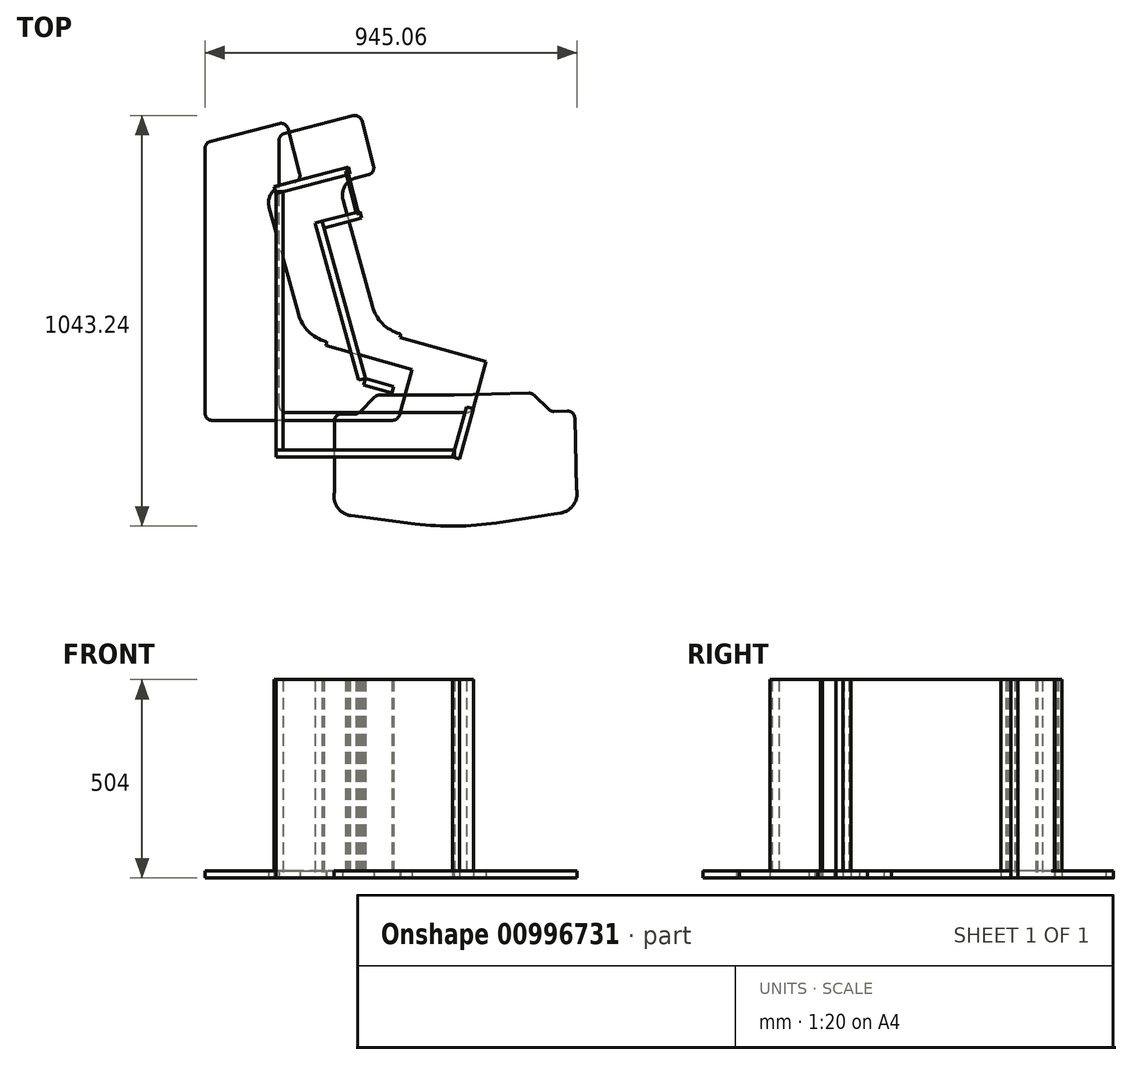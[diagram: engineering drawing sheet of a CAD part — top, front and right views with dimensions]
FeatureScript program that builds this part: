
annotation { "Feature Type Name" : "Feature", "Feature Type Description" : "" }
export const myFeature = defineFeature(function(context is Context, id is Id, definition is map)
    precondition{}
    {
        {
            var Q0;
            Q0=qCreatedBy(makeId("Top.planeOp"),FACE);
            var sketch = newSketch(context, id + "F0", { "sketchPlane" : qUnion([Q0])});
            skLineSegment(sketch, "E0", {"start": v(6.37, 0) * mm, "end": v(-452, 0) * mm});
            skLineSegment(sketch, "E1", {"start": v(-470, 18) * mm, "end": v(-470, 691.14) * mm});
            skArc(sketch, "E2.filletArc", {"start": v(-470, 18) * mm, "mid": v(-464.73, 5.27) * mm, "end": v(-452, 0) * mm});
            skPoint(sketch, "E3.visualSharp", {"position": v(-325.33, 755) * mm});
            skLineSegment(sketch, "E4", {"start": v(-470, 18) * mm, "end": v(-470, 379.49) * mm});
            skLineSegment(sketch, "E5", {"start": v(-470, 379.49) * mm, "end": v(-470, 508.49) * mm});
            skLineSegment(sketch, "E6", {"start": v(-307.17, 540.54) * mm, "end": v(-232.7, 269.91) * mm});
            skLineSegment(sketch, "E7", {"start": v(-264.5, 385.5) * mm, "end": v(-300, 514.5) * mm});
            skLineSegment(sketch, "E8", {"start": v(-470, 18) * mm, "end": v(-470, 175.49) * mm});
            skLineSegment(sketch, "E9", {"start": v(56.32, 128.98) * mm, "end": v(23.7, 13.12) * mm});
            skPoint(sketch, "E10.visualSharp", {"position": v(20, 0) * mm});
            skPoint(sketch, "E11.orphan", {"position": v(-70.83, 811.56) * mm});
            skLineSegment(sketch, "E12.0", {"start": v(-455, 27) * mm, "end": v(-455, 683.67) * mm, "construction": true});
            skLineSegment(sketch, "E13.0", {"start": v(-459.52, 696.42) * mm, "end": v(-270.78, 745.42) * mm, "construction": true});
            skLineSegment(sketch, "E14.0", {"start": v(-456.52, 708.56) * mm, "end": v(-281.29, 754.05) * mm});
            skLineSegment(sketch, "E15", {"start": v(-459.52, 696.42) * mm, "end": v(-455, 679) * mm, "construction": true});
            skLineSegment(sketch, "E16.0", {"start": v(-437, 27) * mm, "end": v(-437, 679) * mm, "construction": true});
            skLineSegment(sketch, "E17", {"start": v(-455, 679) * mm, "end": v(-437, 679) * mm, "construction": true});
            skPoint(sketch, "E18.visualSharp", {"position": v(-470, 705.06) * mm});
            skArc(sketch, "E18.filletArc", {"start": v(-456.52, 708.56) * mm, "mid": v(-466.24, 702.15) * mm, "end": v(-470, 691.14) * mm});
            skLineSegment(sketch, "E19", {"start": v(-237.1, 615.72) * mm, "end": v(-270.78, 745.42) * mm, "construction": true});
            skLineSegment(sketch, "E20.0", {"start": v(-229.56, 626.46) * mm, "end": v(-259.34, 741.15) * mm});
            skPoint(sketch, "E21.visualSharp", {"position": v(-263.87, 758.58) * mm});
            skArc(sketch, "E21.filletArc", {"start": v(-259.34, 741.15) * mm, "mid": v(-267.64, 752.15) * mm, "end": v(-281.29, 754.05) * mm});
            skLineSegment(sketch, "E22", {"start": v(-266.26, 728) * mm, "end": v(-271.1, 726.74) * mm, "construction": true});
            skLineSegment(sketch, "E23.0", {"start": v(-275.09, 596.04) * mm, "end": v(-242.46, 604.51) * mm});
            skLineSegment(sketch, "E24.0", {"start": v(-332.94, 590.84) * mm, "end": v(-237.1, 615.72) * mm, "construction": true});
            skLineSegment(sketch, "E25.0", {"start": v(-355.14, 603.67) * mm, "end": v(-251.31, 630.63) * mm, "construction": true});
            skLineSegment(sketch, "E26.0", {"start": v(-337.71, 608.2) * mm, "end": v(-227.85, 209) * mm, "construction": true});
            skLineSegment(sketch, "E27.0", {"start": v(-355.07, 603.42) * mm, "end": v(-245.28, 204.47) * mm, "construction": true});
            skPoint(sketch, "E28.visualSharp", {"position": v(-225.04, 609.03) * mm});
            skArc(sketch, "E28.filletArc", {"start": v(-242.46, 604.51) * mm, "mid": v(-231.47, 612.81) * mm, "end": v(-229.56, 626.46) * mm});
            skPoint(sketch, "E29.visualSharp", {"position": v(-319.28, 584.57) * mm});
            skArc(sketch, "E30.filletArc", {"start": v(-275.09, 596.04) * mm, "mid": v(-302.74, 575) * mm, "end": v(-307.17, 540.54) * mm});
            skLineSegment(sketch, "E31.0", {"start": v(-245.28, 204.47) * mm, "end": v(-227.85, 209) * mm, "construction": true});
            skLineSegment(sketch, "E32", {"start": v(-160, 189.88) * mm, "end": v(-155.66, 188.66) * mm});
            skLineSegment(sketch, "E33.0", {"start": v(-232.73, 191.66) * mm, "end": v(-160.54, 171.34) * mm, "construction": true});
            skLineSegment(sketch, "E34", {"start": v(-227.85, 209) * mm, "end": v(-155.66, 188.66) * mm, "construction": true});
            skLineSegment(sketch, "E35", {"start": v(-227.85, 209) * mm, "end": v(-232.73, 191.66) * mm, "construction": true});
            skLineSegment(sketch, "E36.0", {"start": v(-163.8, 200.3) * mm, "end": v(-163.38, 200.19) * mm});
            skLineSegment(sketch, "E37", {"start": v(-155.66, 188.66) * mm, "end": v(-160.54, 171.34) * mm, "construction": true});
            skLineSegment(sketch, "E38", {"start": v(-155.66, 188.66) * mm, "end": v(56.32, 128.98) * mm});
            skArc(sketch, "E39.filletArc", {"start": v(-232.7, 269.91) * mm, "mid": v(-207.2, 225.94) * mm, "end": v(-163.38, 200.19) * mm});
            skLineSegment(sketch, "E40.0", {"start": v(-162.43, 197.84) * mm, "end": v(-164.32, 191.1) * mm});
            skLineSegment(sketch, "E41.0", {"start": v(46.7, 131.7) * mm, "end": v(10.77, 4.11) * mm, "construction": true});
            skArc(sketch, "E42.filletArc", {"start": v(6.37, 0) * mm, "mid": v(17.24, 3.65) * mm, "end": v(23.7, 13.12) * mm});
            skLineSegment(sketch, "E43.0", {"start": v(29.36, 136.57) * mm, "end": v(-6.56, 9) * mm, "construction": true});
            skLineSegment(sketch, "E44", {"start": v(-160.54, 171.34) * mm, "end": v(-160.54, 171.34) * mm});
            skLineSegment(sketch, "E45", {"start": v(-455, 27) * mm, "end": v(-455, 9) * mm, "construction": true});
            skLineSegment(sketch, "E46.0", {"start": v(-1.49, 9) * mm, "end": v(-455, 9) * mm, "construction": true});
            skLineSegment(sketch, "E47.0", {"start": v(-7, 27) * mm, "end": v(-7, 9) * mm, "construction": true});
            skLineSegment(sketch, "E48", {"start": v(-437, 679) * mm, "end": v(-437, 683.67) * mm, "construction": true});
            skLineSegment(sketch, "E49", {"start": v(-1.49, 27) * mm, "end": v(-455, 27) * mm, "construction": true});
            skLineSegment(sketch, "E50", {"start": v(-1.49, 27) * mm, "end": v(-1.49, 9) * mm, "construction": true});
            skLineSegment(sketch, "E51", {"start": v(-6.56, 9) * mm, "end": v(10.77, 4.11) * mm, "construction": true});
            skLineSegment(sketch, "E52", {"start": v(-437, 683.67) * mm, "end": v(-455, 683.67) * mm, "construction": true});
            skLineSegment(sketch, "E53", {"start": v(-1.49, 9) * mm, "end": v(12.14, 9) * mm, "construction": true});
            skLineSegment(sketch, "E54.0", {"start": v(-241.95, 614.46) * mm, "end": v(-275.62, 744.16) * mm, "construction": true});
            skLineSegment(sketch, "E55.0", {"start": v(-246.79, 613.2) * mm, "end": v(-280.46, 742.9) * mm, "construction": true});
            skLineSegment(sketch, "E56", {"start": v(-246.47, 631.88) * mm, "end": v(-241.63, 633.14) * mm, "construction": true});
            skLineSegment(sketch, "E57", {"start": v(-275.94, 725.48) * mm, "end": v(-455, 679) * mm, "construction": true});
            skLineSegment(sketch, "E58.0", {"start": v(-273.6, 736.42) * mm, "end": v(-278.45, 735.16) * mm, "construction": true});
            skLineSegment(sketch, "E59.0", {"start": v(-250.05, 625.79) * mm, "end": v(-245.21, 627.04) * mm, "construction": true});
            skLineSegment(sketch, "E60.0", {"start": v(-272.35, 731.58) * mm, "end": v(-277.2, 730.32) * mm, "construction": true});
            skLineSegment(sketch, "E61", {"start": v(-164.32, 191.1) * mm, "end": v(-155.66, 188.66) * mm});
            skPoint(sketch, "E62.visualSharp", {"position": v(-161.88, 199.77) * mm});
            skArc(sketch, "E62.filletArc", {"start": v(-162.43, 197.84) * mm, "mid": v(-162.6, 199.36) * mm, "end": v(-163.8, 200.3) * mm});
            skSolve(sketch);
        }
        {
            var Q0;
            Q0=qCreatedBy(makeId("Top.planeOp"),FACE);
            var sketch = newSketch(context, id + "F1", { "sketchPlane" : qUnion([Q0])});
            skLineSegment(sketch, "E63.0", {"start": v(-227.85, 209) * mm, "end": v(-232.73, 191.66) * mm});
            skLineSegment(sketch, "E64.0", {"start": v(-227.85, 209) * mm, "end": v(-155.66, 188.66) * mm});
            skLineSegment(sketch, "E64.1", {"start": v(-232.73, 191.66) * mm, "end": v(-160.54, 171.34) * mm});
            skLineSegment(sketch, "E64.2", {"start": v(-155.66, 188.66) * mm, "end": v(-160.54, 171.34) * mm});
            skSolve(sketch);
        }
        {
            var Q0;
            Q0=qCreatedBy(makeId("Top.planeOp"),FACE);
            var sketch = newSketch(context, id + "F2", { "sketchPlane" : qUnion([Q0])});
            skLineSegment(sketch, "E65.0", {"start": v(-266.26, 728) * mm, "end": v(-270.78, 745.42) * mm});
            skLineSegment(sketch, "E65.1", {"start": v(-273.6, 736.42) * mm, "end": v(-278.45, 735.16) * mm});
            skLineSegment(sketch, "E65.3", {"start": v(-271.1, 726.74) * mm, "end": v(-273.6, 736.42) * mm});
            skLineSegment(sketch, "E65.4", {"start": v(-275.94, 725.48) * mm, "end": v(-278.45, 735.16) * mm});
            skLineSegment(sketch, "E65.5", {"start": v(-266.26, 728) * mm, "end": v(-271.1, 726.74) * mm});
            skLineSegment(sketch, "E65.6", {"start": v(-459.52, 696.42) * mm, "end": v(-270.78, 745.42) * mm});
            skLineSegment(sketch, "E65.7", {"start": v(-275.94, 725.48) * mm, "end": v(-455, 679) * mm});
            skLineSegment(sketch, "E65.8", {"start": v(-459.52, 696.42) * mm, "end": v(-455, 679) * mm});
            skLineSegment(sketch, "E65.9", {"start": v(-437, 683.67) * mm, "end": v(-455, 683.67) * mm, "construction": true});
            skLineSegment(sketch, "E65.10", {"start": v(-455, 679) * mm, "end": v(-455, 683.67) * mm, "construction": true});
            skSolve(sketch);
        }
        {
            var Q0;
            Q0=qCreatedBy(makeId("Top.planeOp"),FACE);
            var sketch = newSketch(context, id + "F3", { "sketchPlane" : qUnion([Q0])});
            skLineSegment(sketch, "E66.0", {"start": v(-332.94, 590.84) * mm, "end": v(-237.1, 615.72) * mm});
            skLineSegment(sketch, "E66.1", {"start": v(-337.71, 608.2) * mm, "end": v(-332.94, 590.84) * mm});
            skLineSegment(sketch, "E66.2", {"start": v(-337.71, 608.2) * mm, "end": v(-251.31, 630.63) * mm});
            skLineSegment(sketch, "E66.3", {"start": v(-250.05, 625.79) * mm, "end": v(-251.31, 630.63) * mm});
            skLineSegment(sketch, "E66.4", {"start": v(-245.21, 627.04) * mm, "end": v(-246.47, 631.88) * mm});
            skLineSegment(sketch, "E66.5", {"start": v(-237.1, 615.72) * mm, "end": v(-241.63, 633.14) * mm});
            skLineSegment(sketch, "E66.6", {"start": v(-246.47, 631.88) * mm, "end": v(-241.63, 633.14) * mm});
            skLineSegment(sketch, "E66.7", {"start": v(-250.05, 625.79) * mm, "end": v(-245.21, 627.04) * mm});
            skPoint(sketch, "E67.orphan", {"position": v(-227.85, 209) * mm});
            skSolve(sketch);
        }
        {
            var Q0;
            Q0=qCreatedBy(makeId("Top.planeOp"),FACE);
            var sketch = newSketch(context, id + "F4", { "sketchPlane" : qUnion([Q0])});
            skLineSegment(sketch, "E68.0", {"start": v(-1.49, 27) * mm, "end": v(-455, 27) * mm});
            skLineSegment(sketch, "E68.1", {"start": v(-455, 27) * mm, "end": v(-455, 9) * mm});
            skLineSegment(sketch, "E68.2", {"start": v(-1.49, 9) * mm, "end": v(-455, 9) * mm});
            skLineSegment(sketch, "E68.3", {"start": v(-1.49, 27) * mm, "end": v(-1.49, 9) * mm});
            skLineSegment(sketch, "E68.4", {"start": v(-1.49, 27) * mm, "end": v(-6.56, 9) * mm, "construction": true});
            skPoint(sketch, "E68.5.end.orphan", {"position": v(-7, 9) * mm});
            skSolve(sketch);
        }
        {
            var Q0;
            Q0=qCreatedBy(makeId("Top.planeOp"),FACE);
            var sketch = newSketch(context, id + "F5", { "sketchPlane" : qUnion([Q0])});
            skLineSegment(sketch, "E69.0", {"start": v(-355.14, 603.67) * mm, "end": v(-245.28, 204.47) * mm});
            skLineSegment(sketch, "E69.1", {"start": v(-355.14, 603.67) * mm, "end": v(-337.71, 608.2) * mm});
            skLineSegment(sketch, "E69.2", {"start": v(-337.71, 608.2) * mm, "end": v(-227.85, 209) * mm});
            skLineSegment(sketch, "E69.3", {"start": v(-245.28, 204.47) * mm, "end": v(-227.85, 209) * mm});
            skSolve(sketch);
        }
        {
            var Q0;
            Q0=qCreatedBy(makeId("Top.planeOp"),FACE);
            var sketch = newSketch(context, id + "F6", { "sketchPlane" : qUnion([Q0])});
            skLineSegment(sketch, "E70.0", {"start": v(-437, 683.67) * mm, "end": v(-455, 683.67) * mm});
            skLineSegment(sketch, "E70.2", {"start": v(-437, 683.67) * mm, "end": v(-455, 679) * mm, "construction": true});
            skLineSegment(sketch, "E70.3", {"start": v(-437, 27) * mm, "end": v(-437, 679) * mm});
            skLineSegment(sketch, "E70.4", {"start": v(-455, 27) * mm, "end": v(-455, 683.67) * mm});
            skLineSegment(sketch, "E70.5", {"start": v(-437, 27) * mm, "end": v(-455, 27) * mm});
            skLineSegment(sketch, "E70.6", {"start": v(-437, 679) * mm, "end": v(-437, 683.67) * mm});
            skPoint(sketch, "E70.1.start.orphan", {"position": v(-455, 679) * mm});
            skSolve(sketch);
        }
        {
            var Q0;
            Q0=qCreatedBy(makeId("Top.planeOp"),FACE);
            var sketch = newSketch(context, id + "F7", { "sketchPlane" : qUnion([Q0])});
            skLineSegment(sketch, "E71.0", {"start": v(29.36, 136.57) * mm, "end": v(-6.56, 9) * mm});
            skLineSegment(sketch, "E71.1", {"start": v(46.7, 131.7) * mm, "end": v(10.77, 4.11) * mm});
            skLineSegment(sketch, "E71.2", {"start": v(29.36, 136.57) * mm, "end": v(46.7, 131.7) * mm});
            skLineSegment(sketch, "E71.3", {"start": v(-1.49, 9) * mm, "end": v(12.14, 9) * mm, "construction": true});
            skLineSegment(sketch, "E71.4", {"start": v(-1.49, 9) * mm, "end": v(-6.56, 9) * mm, "construction": true});
            skLineSegment(sketch, "E71.5", {"start": v(-1.49, 27) * mm, "end": v(-1.49, 9) * mm, "construction": true});
            skLineSegment(sketch, "E71.6", {"start": v(-6.56, 9) * mm, "end": v(10.77, 4.11) * mm});
            skSolve(sketch);
        }
        {
            var Q0;
            Q0=qCreatedBy(makeId("Top.planeOp"),FACE);
            var sketch = newSketch(context, id + "F8", { "sketchPlane" : qUnion([Q0])});
            skLineSegment(sketch, "E72.0", {"start": v(-250.05, 625.79) * mm, "end": v(-277.2, 730.32) * mm});
            skLineSegment(sketch, "E72.1", {"start": v(-245.21, 627.04) * mm, "end": v(-272.35, 731.58) * mm});
            skLineSegment(sketch, "E72.2", {"start": v(-272.35, 731.58) * mm, "end": v(-277.2, 730.32) * mm});
            skLineSegment(sketch, "E72.3", {"start": v(-250.05, 625.79) * mm, "end": v(-245.21, 627.04) * mm});
            skSolve(sketch);
        }
        {
            var Q0;
            Q0=qCreatedBy(makeId("Top.planeOp"),FACE);
            var sketch = newSketch(context, id + "F9", { "sketchPlane" : qUnion([Q0])});
            skLineSegment(sketch, "E73", {"start": v(28.99, 122.08) * mm, "end": v(-429.38, 122.08) * mm});
            skLineSegment(sketch, "E74", {"start": v(-447.38, 140.08) * mm, "end": v(-447.38, 813.21) * mm});
            skArc(sketch, "E75.filletArc", {"start": v(-447.38, 140.08) * mm, "mid": v(-442.1, 127.35) * mm, "end": v(-429.38, 122.08) * mm});
            skLineSegment(sketch, "E76", {"start": v(-447.38, 140.08) * mm, "end": v(-447.38, 501.56) * mm});
            skLineSegment(sketch, "E77", {"start": v(-447.38, 501.56) * mm, "end": v(-447.38, 630.56) * mm});
            skLineSegment(sketch, "E78", {"start": v(-284.55, 662.62) * mm, "end": v(-210.07, 391.99) * mm});
            skLineSegment(sketch, "E79", {"start": v(-241.88, 507.58) * mm, "end": v(-277.38, 636.58) * mm});
            skLineSegment(sketch, "E80", {"start": v(-447.38, 140.08) * mm, "end": v(-447.38, 297.56) * mm});
            skLineSegment(sketch, "E81", {"start": v(78.93, 251.06) * mm, "end": v(46.31, 135.2) * mm});
            skLineSegment(sketch, "E82.0", {"start": v(-432.38, 149.07) * mm, "end": v(-432.38, 805.74) * mm, "construction": true});
            skLineSegment(sketch, "E83.0", {"start": v(-436.9, 818.5) * mm, "end": v(-248.16, 867.5) * mm, "construction": true});
            skLineSegment(sketch, "E84.0", {"start": v(-433.9, 830.63) * mm, "end": v(-258.67, 876.13) * mm});
            skLineSegment(sketch, "E85", {"start": v(-436.9, 818.5) * mm, "end": v(-432.38, 801.07) * mm, "construction": true});
            skLineSegment(sketch, "E86.0", {"start": v(-414.38, 149.07) * mm, "end": v(-414.38, 801.07) * mm, "construction": true});
            skLineSegment(sketch, "E87", {"start": v(-432.38, 801.07) * mm, "end": v(-414.38, 801.07) * mm, "construction": true});
            skArc(sketch, "E88.filletArc", {"start": v(-433.9, 830.63) * mm, "mid": v(-443.62, 824.23) * mm, "end": v(-447.38, 813.21) * mm});
            skLineSegment(sketch, "E89", {"start": v(-214.49, 737.8) * mm, "end": v(-248.16, 867.5) * mm, "construction": true});
            skLineSegment(sketch, "E90.0", {"start": v(-206.95, 748.53) * mm, "end": v(-236.72, 863.23) * mm});
            skArc(sketch, "E91.filletArc", {"start": v(-236.72, 863.23) * mm, "mid": v(-245.02, 874.22) * mm, "end": v(-258.67, 876.13) * mm});
            skLineSegment(sketch, "E92", {"start": v(-243.64, 850.07) * mm, "end": v(-248.48, 848.81) * mm, "construction": true});
            skLineSegment(sketch, "E93.0", {"start": v(-252.47, 718.12) * mm, "end": v(-219.85, 726.59) * mm});
            skLineSegment(sketch, "E94.0", {"start": v(-310.32, 712.91) * mm, "end": v(-214.49, 737.8) * mm, "construction": true});
            skLineSegment(sketch, "E95.0", {"start": v(-332.52, 725.75) * mm, "end": v(-228.7, 752.7) * mm, "construction": true});
            skLineSegment(sketch, "E96.0", {"start": v(-315.1, 730.27) * mm, "end": v(-205.24, 331.07) * mm, "construction": true});
            skLineSegment(sketch, "E97.0", {"start": v(-332.45, 725.5) * mm, "end": v(-222.66, 326.54) * mm, "construction": true});
            skArc(sketch, "E98.filletArc", {"start": v(-219.85, 726.59) * mm, "mid": v(-208.85, 734.89) * mm, "end": v(-206.95, 748.53) * mm});
            skArc(sketch, "E99.filletArc", {"start": v(-252.47, 718.12) * mm, "mid": v(-280.12, 697.08) * mm, "end": v(-284.55, 662.62) * mm});
            skLineSegment(sketch, "E100.0", {"start": v(-222.66, 326.54) * mm, "end": v(-205.24, 331.07) * mm, "construction": true});
            skLineSegment(sketch, "E101", {"start": v(-137.37, 311.96) * mm, "end": v(-133.04, 310.74) * mm});
            skLineSegment(sketch, "E102.0", {"start": v(-210.11, 313.74) * mm, "end": v(-137.92, 293.41) * mm, "construction": true});
            skLineSegment(sketch, "E103", {"start": v(-205.24, 331.07) * mm, "end": v(-133.04, 310.74) * mm, "construction": true});
            skLineSegment(sketch, "E104", {"start": v(-205.24, 331.07) * mm, "end": v(-210.11, 313.74) * mm, "construction": true});
            skLineSegment(sketch, "E105.0", {"start": v(-140.76, 322.26) * mm, "end": v(-139.67, 321.95) * mm});
            skLineSegment(sketch, "E106", {"start": v(-133.04, 310.74) * mm, "end": v(-137.92, 293.41) * mm, "construction": true});
            skLineSegment(sketch, "E107", {"start": v(-133.04, 310.74) * mm, "end": v(78.93, 251.06) * mm});
            skArc(sketch, "E108.filletArc", {"start": v(-210.07, 391.99) * mm, "mid": v(-184.58, 348.02) * mm, "end": v(-140.76, 322.26) * mm});
            skLineSegment(sketch, "E109.0", {"start": v(-138.28, 319.49) * mm, "end": v(-139.39, 315.56) * mm});
            skLineSegment(sketch, "E110.0", {"start": v(69.3, 253.77) * mm, "end": v(33.39, 126.2) * mm, "construction": true});
            skArc(sketch, "E111.filletArc", {"start": v(28.99, 122.08) * mm, "mid": v(39.85, 125.73) * mm, "end": v(46.31, 135.2) * mm});
            skLineSegment(sketch, "E112.0", {"start": v(51.98, 258.64) * mm, "end": v(16.06, 131.07) * mm, "construction": true});
            skLineSegment(sketch, "E113", {"start": v(-432.38, 149.07) * mm, "end": v(-432.38, 131.07) * mm, "construction": true});
            skLineSegment(sketch, "E114.0", {"start": v(21.13, 131.07) * mm, "end": v(-432.38, 131.07) * mm, "construction": true});
            skLineSegment(sketch, "E115.0", {"start": v(15.62, 149.07) * mm, "end": v(15.62, 131.07) * mm, "construction": true});
            skLineSegment(sketch, "E116", {"start": v(-414.38, 801.07) * mm, "end": v(-414.38, 805.74) * mm, "construction": true});
            skLineSegment(sketch, "E117", {"start": v(21.13, 149.07) * mm, "end": v(-432.38, 149.07) * mm, "construction": true});
            skLineSegment(sketch, "E118", {"start": v(21.13, 149.07) * mm, "end": v(21.13, 131.07) * mm, "construction": true});
            skLineSegment(sketch, "E119", {"start": v(16.06, 131.07) * mm, "end": v(33.39, 126.2) * mm, "construction": true});
            skLineSegment(sketch, "E120", {"start": v(-414.38, 805.74) * mm, "end": v(-432.38, 805.74) * mm, "construction": true});
            skLineSegment(sketch, "E121", {"start": v(21.13, 131.07) * mm, "end": v(34.76, 131.07) * mm, "construction": true});
            skLineSegment(sketch, "E122.0", {"start": v(-219.33, 736.54) * mm, "end": v(-253, 866.24) * mm, "construction": true});
            skLineSegment(sketch, "E123.0", {"start": v(-224.17, 735.28) * mm, "end": v(-257.84, 864.98) * mm, "construction": true});
            skLineSegment(sketch, "E124", {"start": v(-223.85, 753.96) * mm, "end": v(-219.01, 755.21) * mm, "construction": true});
            skLineSegment(sketch, "E125", {"start": v(-253.32, 847.56) * mm, "end": v(-432.38, 801.07) * mm, "construction": true});
            skLineSegment(sketch, "E126.0", {"start": v(-251, 858.5) * mm, "end": v(-255.83, 857.24) * mm, "construction": true});
            skLineSegment(sketch, "E127.0", {"start": v(-227.44, 747.86) * mm, "end": v(-222.6, 749.12) * mm, "construction": true});
            skLineSegment(sketch, "E128.0", {"start": v(-249.73, 853.65) * mm, "end": v(-254.57, 852.4) * mm, "construction": true});
            skLineSegment(sketch, "E129", {"start": v(-139.39, 315.56) * mm, "end": v(-140.18, 312.75) * mm});
            skLineSegment(sketch, "E130", {"start": v(-140.18, 312.75) * mm, "end": v(-133.04, 310.74) * mm});
            skPoint(sketch, "E131.visualSharp", {"position": v(-137.74, 321.41) * mm});
            skArc(sketch, "E131.filletArc", {"start": v(-138.28, 319.49) * mm, "mid": v(-138.46, 321) * mm, "end": v(-139.67, 321.95) * mm});
            skSolve(sketch);
        }
        {
            var Q0;
            Q0=qCreatedBy(makeId("Top.planeOp"),FACE);
            var sketch = newSketch(context, id + "F10", { "sketchPlane" : qUnion([Q0])});
            skLineSegment(sketch, "E132", {"start": v(-158.86, 102.2) * mm, "end": v(-617.23, 102.2) * mm});
            skLineSegment(sketch, "E133", {"start": v(-635.23, 120.2) * mm, "end": v(-635.23, 793.34) * mm});
            skArc(sketch, "E134.filletArc", {"start": v(-635.23, 120.2) * mm, "mid": v(-629.96, 107.48) * mm, "end": v(-617.23, 102.2) * mm});
            skLineSegment(sketch, "E135", {"start": v(-635.23, 120.2) * mm, "end": v(-635.23, 481.7) * mm});
            skLineSegment(sketch, "E136", {"start": v(-635.23, 481.7) * mm, "end": v(-635.23, 610.7) * mm});
            skLineSegment(sketch, "E137", {"start": v(-472.4, 642.75) * mm, "end": v(-397.92, 372.12) * mm});
            skLineSegment(sketch, "E138", {"start": v(-429.73, 487.7) * mm, "end": v(-465.23, 616.7) * mm});
            skLineSegment(sketch, "E139", {"start": v(-635.23, 120.2) * mm, "end": v(-635.23, 277.7) * mm});
            skLineSegment(sketch, "E140", {"start": v(-108.91, 231.19) * mm, "end": v(-141.53, 115.33) * mm});
            skLineSegment(sketch, "E141.0", {"start": v(-620.23, 129.2) * mm, "end": v(-620.23, 785.87) * mm, "construction": true});
            skLineSegment(sketch, "E142.0", {"start": v(-624.75, 798.62) * mm, "end": v(-436, 847.62) * mm, "construction": true});
            skLineSegment(sketch, "E143.0", {"start": v(-621.75, 810.76) * mm, "end": v(-446.51, 856.26) * mm});
            skLineSegment(sketch, "E144", {"start": v(-624.75, 798.62) * mm, "end": v(-620.23, 781.2) * mm, "construction": true});
            skLineSegment(sketch, "E145.0", {"start": v(-602.23, 129.2) * mm, "end": v(-602.23, 781.2) * mm, "construction": true});
            skLineSegment(sketch, "E146", {"start": v(-620.23, 781.2) * mm, "end": v(-602.23, 781.2) * mm, "construction": true});
            skArc(sketch, "E147.filletArc", {"start": v(-621.75, 810.76) * mm, "mid": v(-631.46, 804.36) * mm, "end": v(-635.23, 793.34) * mm});
            skLineSegment(sketch, "E148", {"start": v(-402.34, 717.92) * mm, "end": v(-436, 847.62) * mm, "construction": true});
            skLineSegment(sketch, "E149.0", {"start": v(-394.8, 728.66) * mm, "end": v(-424.57, 843.36) * mm});
            skArc(sketch, "E150.filletArc", {"start": v(-424.57, 843.36) * mm, "mid": v(-432.87, 854.35) * mm, "end": v(-446.51, 856.26) * mm});
            skLineSegment(sketch, "E151", {"start": v(-431.48, 830.2) * mm, "end": v(-436.32, 828.94) * mm, "construction": true});
            skLineSegment(sketch, "E152.0", {"start": v(-440.32, 698.25) * mm, "end": v(-407.7, 706.72) * mm});
            skLineSegment(sketch, "E153.0", {"start": v(-498.16, 693.04) * mm, "end": v(-402.34, 717.92) * mm, "construction": true});
            skLineSegment(sketch, "E154.0", {"start": v(-520.36, 705.88) * mm, "end": v(-416.54, 732.83) * mm, "construction": true});
            skLineSegment(sketch, "E155.0", {"start": v(-502.94, 710.4) * mm, "end": v(-393.08, 311.2) * mm, "construction": true});
            skLineSegment(sketch, "E156.0", {"start": v(-520.3, 705.62) * mm, "end": v(-410.5, 306.67) * mm, "construction": true});
            skArc(sketch, "E157.filletArc", {"start": v(-407.7, 706.72) * mm, "mid": v(-396.7, 715.02) * mm, "end": v(-394.8, 728.66) * mm});
            skArc(sketch, "E158.filletArc", {"start": v(-440.32, 698.25) * mm, "mid": v(-467.97, 677.21) * mm, "end": v(-472.4, 642.75) * mm});
            skLineSegment(sketch, "E159.0", {"start": v(-410.5, 306.67) * mm, "end": v(-393.08, 311.2) * mm, "construction": true});
            skLineSegment(sketch, "E160", {"start": v(-325.22, 292.09) * mm, "end": v(-320.89, 290.87) * mm});
            skLineSegment(sketch, "E161.0", {"start": v(-397.96, 293.87) * mm, "end": v(-325.77, 273.54) * mm, "construction": true});
            skLineSegment(sketch, "E162", {"start": v(-393.08, 311.2) * mm, "end": v(-320.89, 290.87) * mm, "construction": true});
            skLineSegment(sketch, "E163", {"start": v(-393.08, 311.2) * mm, "end": v(-397.96, 293.87) * mm, "construction": true});
            skLineSegment(sketch, "E164.0", {"start": v(-328.6, 302.4) * mm, "end": v(-327.61, 302.11) * mm});
            skLineSegment(sketch, "E165", {"start": v(-320.89, 290.87) * mm, "end": v(-325.77, 273.54) * mm, "construction": true});
            skLineSegment(sketch, "E166", {"start": v(-320.89, 290.87) * mm, "end": v(-108.91, 231.19) * mm});
            skArc(sketch, "E167.filletArc", {"start": v(-397.92, 372.12) * mm, "mid": v(-372.42, 328.15) * mm, "end": v(-328.6, 302.4) * mm});
            skLineSegment(sketch, "E168.0", {"start": v(-326.23, 299.65) * mm, "end": v(-327.3, 295.81) * mm});
            skLineSegment(sketch, "E169.0", {"start": v(-118.54, 233.9) * mm, "end": v(-154.46, 106.32) * mm, "construction": true});
            skArc(sketch, "E170.filletArc", {"start": v(-158.86, 102.2) * mm, "mid": v(-148, 105.86) * mm, "end": v(-141.53, 115.33) * mm});
            skLineSegment(sketch, "E171.0", {"start": v(-135.86, 238.77) * mm, "end": v(-171.78, 111.2) * mm, "construction": true});
            skLineSegment(sketch, "E172", {"start": v(-620.23, 129.2) * mm, "end": v(-620.23, 111.2) * mm, "construction": true});
            skLineSegment(sketch, "E173.0", {"start": v(-166.72, 111.2) * mm, "end": v(-620.23, 111.2) * mm, "construction": true});
            skLineSegment(sketch, "E174.0", {"start": v(-172.23, 129.2) * mm, "end": v(-172.23, 111.2) * mm, "construction": true});
            skLineSegment(sketch, "E175", {"start": v(-602.23, 781.2) * mm, "end": v(-602.23, 785.87) * mm, "construction": true});
            skLineSegment(sketch, "E176", {"start": v(-166.72, 129.2) * mm, "end": v(-620.23, 129.2) * mm, "construction": true});
            skLineSegment(sketch, "E177", {"start": v(-166.72, 129.2) * mm, "end": v(-166.72, 111.2) * mm, "construction": true});
            skLineSegment(sketch, "E178", {"start": v(-171.78, 111.2) * mm, "end": v(-154.46, 106.32) * mm, "construction": true});
            skLineSegment(sketch, "E179", {"start": v(-602.23, 785.87) * mm, "end": v(-620.23, 785.87) * mm, "construction": true});
            skLineSegment(sketch, "E180", {"start": v(-166.72, 111.2) * mm, "end": v(-153.08, 111.2) * mm, "construction": true});
            skLineSegment(sketch, "E181.0", {"start": v(-407.17, 716.67) * mm, "end": v(-440.85, 846.37) * mm, "construction": true});
            skLineSegment(sketch, "E182.0", {"start": v(-412.01, 715.4) * mm, "end": v(-445.69, 845.1) * mm, "construction": true});
            skLineSegment(sketch, "E183", {"start": v(-411.7, 734.09) * mm, "end": v(-406.86, 735.34) * mm, "construction": true});
            skLineSegment(sketch, "E184", {"start": v(-441.16, 827.69) * mm, "end": v(-620.23, 781.2) * mm, "construction": true});
            skLineSegment(sketch, "E185.0", {"start": v(-438.84, 838.62) * mm, "end": v(-443.68, 837.37) * mm, "construction": true});
            skLineSegment(sketch, "E186.0", {"start": v(-415.28, 728) * mm, "end": v(-410.44, 729.25) * mm, "construction": true});
            skLineSegment(sketch, "E187.0", {"start": v(-437.58, 833.78) * mm, "end": v(-442.42, 832.53) * mm, "construction": true});
            skLineSegment(sketch, "E188", {"start": v(-327.3, 295.81) * mm, "end": v(-328.12, 292.9) * mm});
            skLineSegment(sketch, "E189", {"start": v(-328.12, 292.9) * mm, "end": v(-320.89, 290.87) * mm});
            skPoint(sketch, "E190.visualSharp", {"position": v(-325.69, 301.57) * mm});
            skArc(sketch, "E190.filletArc", {"start": v(-326.23, 299.65) * mm, "mid": v(-326.4, 301.17) * mm, "end": v(-327.61, 302.11) * mm});
            skSolve(sketch);
        }
        {
            var Q0;
            Q0=qCreatedBy(makeId("Top.planeOp"),FACE);
            var sketch = newSketch(context, id + "F11", { "sketchPlane" : qUnion([Q0])});
            skPoint(sketch, "E191.middle", {"position": v(0, 0) * mm});
            skLineSegment(sketch, "E192", {"start": v(-2.11, 166.5) * mm, "end": v(0.6, -46.87) * mm});
            skLineSegment(sketch, "E193", {"start": v(-191.57, 166.5) * mm, "end": v(-2.11, 166.5) * mm});
            skLineSegment(sketch, "E194", {"start": v(-288.8, 118.5) * mm, "end": v(-254.11, 118.5) * mm});
            skLineSegment(sketch, "E195", {"start": v(-241.32, 123.84) * mm, "end": v(-204.36, 161.16) * mm});
            skLineSegment(sketch, "E196", {"start": v(-306.8, -81.5) * mm, "end": v(-306.8, 100.5) * mm});
            skArc(sketch, "E197", {"start": v(-306.8, -81.5) * mm, "mid": v(-297.95, -120.02) * mm, "end": v(-263.89, -140.07) * mm});
            skLineSegment(sketch, "E198", {"start": v(-101.51, -160.6) * mm, "end": v(-263.89, -140.07) * mm});
            skPoint(sketch, "E199.orphan", {"position": v(-310, -166.5) * mm});
            skPoint(sketch, "E191.top.start.orphan", {"position": v(-312.11, 166.5) * mm});
            skPoint(sketch, "E200.start.orphan", {"position": v(-246.6, 166.5) * mm});
            skPoint(sketch, "E191.right.end.orphan", {"position": v(310, 166.5) * mm});
            skPoint(sketch, "E191.bottom.end.orphan", {"position": v(312.11, -166.5) * mm});
            skLineSegment(sketch, "E201.MirrorCS", {"start": v(187.28, 171.31) * mm, "end": v(-2.11, 166.5) * mm});
            skLineSegment(sketch, "E202.MirrorCS", {"start": v(238.1, 129.92) * mm, "end": v(200.2, 166.3) * mm});
            skLineSegment(sketch, "E203.MirrorCS", {"start": v(285.7, 125.8) * mm, "end": v(251.02, 124.91) * mm});
            skLineSegment(sketch, "E204.MirrorCS", {"start": v(308.77, -73.68) * mm, "end": v(304.15, 108.26) * mm});
            skArc(sketch, "E205.MirrorCS", {"start": v(308.77, -73.68) * mm, "mid": v(300.9, -112.41) * mm, "end": v(267.36, -133.33) * mm});
            skLineSegment(sketch, "E206.MirrorCS", {"start": v(105.56, -157.98) * mm, "end": v(267.36, -133.33) * mm});
            skPoint(sketch, "E207.visualSharp", {"position": v(2.2, -173.72) * mm});
            skArc(sketch, "E207.filletArc", {"start": v(-101.51, -160.6) * mm, "mid": v(2.11, -166.47) * mm, "end": v(105.56, -157.98) * mm});
            skPoint(sketch, "E208.visualSharp", {"position": v(-199.08, 166.5) * mm});
            skArc(sketch, "E208.filletArc", {"start": v(-191.57, 166.5) * mm, "mid": v(-198.5, 165.11) * mm, "end": v(-204.36, 161.16) * mm});
            skPoint(sketch, "E209.visualSharp", {"position": v(-246.6, 118.5) * mm});
            skArc(sketch, "E209.filletArc", {"start": v(-254.11, 118.5) * mm, "mid": v(-247.18, 119.89) * mm, "end": v(-241.32, 123.84) * mm});
            skPoint(sketch, "E210.visualSharp", {"position": v(194.8, 171.5) * mm});
            skArc(sketch, "E210.filletArc", {"start": v(200.2, 166.3) * mm, "mid": v(194.25, 170.1) * mm, "end": v(187.28, 171.31) * mm});
            skPoint(sketch, "E211.visualSharp", {"position": v(243.52, 124.72) * mm});
            skArc(sketch, "E211.filletArc", {"start": v(238.1, 129.92) * mm, "mid": v(244.06, 126.13) * mm, "end": v(251.02, 124.91) * mm});
            skPoint(sketch, "E212.visualSharp", {"position": v(303.7, 126.25) * mm});
            skArc(sketch, "E212.filletArc", {"start": v(304.15, 108.26) * mm, "mid": v(298.56, 120.85) * mm, "end": v(285.7, 125.8) * mm});
            skPoint(sketch, "E213.visualSharp", {"position": v(-306.8, 118.5) * mm});
            skArc(sketch, "E213.filletArc", {"start": v(-288.8, 118.5) * mm, "mid": v(-301.53, 113.23) * mm, "end": v(-306.8, 100.5) * mm});
            skSolve(sketch);
        }
        {
            var Q0;
            Q0 = qSketchRegion(id + "F9", true);
            var Q1;
            Q1 = qSketchRegion(id + "F10", true);
            var Q2;
            Q2 = qSketchRegion(id + "F11", true);
            extrude(context, id + "F12", {"entities" : qUnion([Q0, Q1, Q2]), "depth" : 18 * mm, "offsetDistance" : 25 * mm});
        }
        {
            var Q0;
            Q0 = qSketchRegion(id + "F2", true);
            var Q1;
            Q1 = qSketchRegion(id + "F1", true);
            var Q2;
            Q2 = qSketchRegion(id + "F4", true);
            var Q3;
            Q3 = qSketchRegion(id + "F3", true);
            var Q4;
            Q4 = qSketchRegion(id + "F5", true);
            var Q5;
            Q5 = qSketchRegion(id + "F6", true);
            var Q6;
            Q6 = qSketchRegion(id + "F7", true);
            var Q7;
            Q7 = qSketchRegion(id + "F8", true);
            extrude(context, id + "F13", {"entities" : qUnion([Q0, Q1, Q2, Q3, Q4, Q5, Q6, Q7]), "depth" : 504 * mm, "offsetDistance" : 25 * mm});
        }
    });
